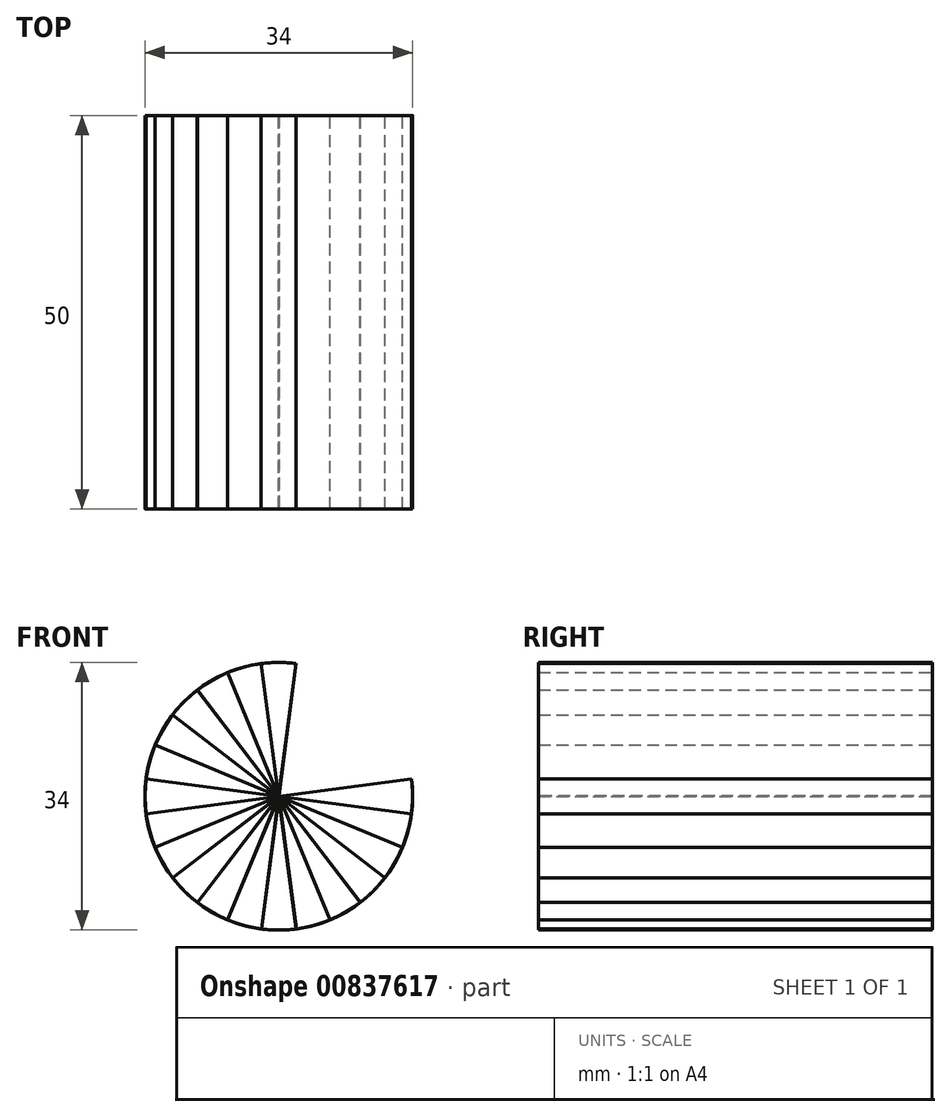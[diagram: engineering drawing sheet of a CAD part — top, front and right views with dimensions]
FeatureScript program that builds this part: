
annotation { "Feature Type Name" : "Feature", "Feature Type Description" : "" }
export const myFeature = defineFeature(function(context is Context, id is Id, definition is map)
    precondition{}
    {
        {
            var Q0;
            Q0=qCreatedBy(makeId("Front.planeOp"),FACE);
            var sketch = newSketch(context, id + "F0", { "sketchPlane" : qUnion([Q0])});
            skCircle(sketch, "E0", {"center": v(-0.33, 0) * mm, "radius": 17 * mm});
            skLineSegment(sketch, "E1", {"start": v(-0.33, 0) * mm, "end": v(-0.33, 0) * mm});
            skLineSegment(sketch, "E2.MirrorCS", {"start": v(-63.33, 0) * mm, "end": v(-17.33, 0) * mm});
            skLineSegment(sketch, "E3.MirrorCS", {"start": v(-61.33, 5.51) * mm, "end": v(-31.1, 1.5) * mm});
            skLineSegment(sketch, "E4.MirrorCS", {"start": v(-61.33, -5.5) * mm, "end": v(-31.1, -1.48) * mm});
            skArc(sketch, "E5.MirrorCS", {"start": v(-31.1, 1.5) * mm, "mid": v(-29.8, 0) * mm, "end": v(-31.1, -1.48) * mm});
            skLineSegment(sketch, "E6.MirrorCS", {"start": v(-61.33, 1.39) * mm, "end": v(-61.33, 5.51) * mm});
            skLineSegment(sketch, "E7.MirrorCS", {"start": v(-63.33, 1.39) * mm, "end": v(-61.33, 1.39) * mm});
            skLineSegment(sketch, "E8.MirrorCS", {"start": v(-63.33, -1.37) * mm, "end": v(-61.33, -1.37) * mm});
            skLineSegment(sketch, "E9.MirrorCS", {"start": v(-61.33, -1.37) * mm, "end": v(-61.33, -5.5) * mm});
            skText(sketch, "E10", { "text": "correct", "fontName": "OpenSans-Regular.ttf"});
            skLineSegment(sketch, "E11.trimOffspring", {"start": v(-17.33, 0) * mm, "end": v(-26.63, 0) * mm});
            skLineSegment(sketch, "E12", {"start": v(-0.33, 0) * mm, "end": v(54.66, 0) * mm});
            skLineSegment(sketch, "E13.MirrorCS", {"start": v(59.97, 9.34) * mm, "end": v(59.45, 13.27) * mm});
            skLineSegment(sketch, "E14.MirrorCS", {"start": v(60.33, 6.6) * mm, "end": v(60.85, 2.67) * mm});
            skLineSegment(sketch, "E15.MirrorCS", {"start": v(60.85, 2.67) * mm, "end": v(30.38, 2.55) * mm});
            skLineSegment(sketch, "E16.MirrorCS", {"start": v(59.45, 13.27) * mm, "end": v(30, 5.5) * mm});
            skArc(sketch, "E17.MirrorCS", {"start": v(30, 5.5) * mm, "mid": v(28.89, 3.86) * mm, "end": v(30.38, 2.55) * mm});
            skLineSegment(sketch, "E18.MirrorCS", {"start": v(62.13, 8.23) * mm, "end": v(-0.33, 0.01) * mm});
            skLineSegment(sketch, "E19.MirrorCS", {"start": v(61.95, 9.6) * mm, "end": v(62.31, 6.87) * mm});
            skLineSegment(sketch, "E20.MirrorCS", {"start": v(62.31, 6.87) * mm, "end": v(60.33, 6.6) * mm});
            skLineSegment(sketch, "E21.MirrorCS", {"start": v(61.95, 9.6) * mm, "end": v(59.97, 9.34) * mm});
            skLineSegment(sketch, "E22.MirrorCS", {"start": v(-0.33, 0) * mm, "end": v(-8.3, 60.49) * mm});
            skArc(sketch, "E23.MirrorCS", {"start": v(-5.82, 30.33) * mm, "mid": v(-4.18, 29.23) * mm, "end": v(-2.87, 30.72) * mm});
            skLineSegment(sketch, "E24.MirrorCS", {"start": v(-13.33, 57.8) * mm, "end": v(-5.82, 30.33) * mm});
            skLineSegment(sketch, "E25.MirrorCS", {"start": v(-2.73, 59.2) * mm, "end": v(-2.87, 30.72) * mm});
            skLineSegment(sketch, "E26.MirrorCS", {"start": v(-9.4, 58.32) * mm, "end": v(-13.33, 57.8) * mm});
            skLineSegment(sketch, "E27.MirrorCS", {"start": v(-9.66, 60.3) * mm, "end": v(-9.4, 58.32) * mm});
            skLineSegment(sketch, "E28.MirrorCS", {"start": v(-6.92, 60.67) * mm, "end": v(-6.66, 58.69) * mm});
            skLineSegment(sketch, "E29.MirrorCS", {"start": v(-6.66, 58.69) * mm, "end": v(-2.73, 59.2) * mm});
            skLineSegment(sketch, "E30", {"start": v(-0.33, 50.96) * mm, "end": v(-0.33, 0) * mm});
            skLineSegment(sketch, "E31.MirrorCS", {"start": v(2.07, 59.2) * mm, "end": v(2.21, 30.72) * mm});
            skArc(sketch, "E32.MirrorCS", {"start": v(5.16, 30.33) * mm, "mid": v(3.52, 29.23) * mm, "end": v(2.21, 30.72) * mm});
            skLineSegment(sketch, "E33.MirrorCS", {"start": v(-0.33, 0) * mm, "end": v(7.63, 60.49) * mm});
            skLineSegment(sketch, "E34.MirrorCS", {"start": v(12.67, 57.8) * mm, "end": v(5.16, 30.33) * mm});
            skLineSegment(sketch, "E35.MirrorCS", {"start": v(6, 58.69) * mm, "end": v(2.07, 59.2) * mm});
            skLineSegment(sketch, "E36.MirrorCS", {"start": v(9, 60.3) * mm, "end": v(8.74, 58.33) * mm});
            skLineSegment(sketch, "E37.MirrorCS", {"start": v(8.74, 58.33) * mm, "end": v(12.67, 57.8) * mm});
            skLineSegment(sketch, "E38.MirrorCS", {"start": v(6.26, 60.67) * mm, "end": v(6, 58.69) * mm});
            skArc(sketch, "E39", {"start": v(-6.92, 60.67) * mm, "mid": v(-0.32, 61.03) * mm, "end": v(6.28, 60.67) * mm});
            const initialGuessF0  = {"E10": [-0.0635, -0.01424, 1, 0, 0.0042]};
            skSetInitialGuess(sketch, initialGuessF0);
            skSolve(sketch);
        }
        {
            var Q0;
            {var subQ7=sQuery(id+"F0.wireOp",EDGE,"E25.MirrorCS");Q0=makeQuery(id+"F0.imprint","IMPRINT",FACE,{"disambiguationData":[TD([[makeQuery(id+"F0.imprint","IMPRINT",EDGE,{"derivedFrom":subQ7}),1.0]])]});}
            var Q1;
            {var subQ0=sQuery(id+"F0.wireOp",EDGE,"E33.MirrorCS");var subQ1=sQuery(id+"F0.wireOp",EDGE,"E0");var subQ2=makeQuery(id+"F0.imprint","INTERSECT",VERTEX,{"derivedFrom":[subQ1,subQ0]});Q1=makeQuery(id+"F0.imprint","IMPRINT",FACE,{"disambiguationData":[TD([[makeQuery(id+"F0.imprint","IMPRINT",EDGE,{"disambiguationData":[TD([[subQ2,-1.0]])],"derivedFrom":subQ1}),-1.0]])]});}
            var Q2;
            {var subQ1=sQuery(id+"F0.wireOp",EDGE,"E0");var subQ5=makeQuery(id+"F0.imprint","INTERSECT",VERTEX,{"derivedFrom":[subQ1,sQuery(id+"F0.wireOp",EDGE,"E11.trimOffspring")]});Q2=makeQuery(id+"F0.imprint","IMPRINT",FACE,{"disambiguationData":[TD([[makeQuery(id+"F0.imprint","IMPRINT",EDGE,{"disambiguationData":[TD([[subQ5,1.0]])],"derivedFrom":subQ1}),1.0]])]});}
            var Q3;
            {var subQ0=sQuery(id+"F0.wireOp",EDGE,"E30");var subQ1=sQuery(id+"F0.wireOp",EDGE,"E0");var subQ2=makeQuery(id+"F0.imprint","INTERSECT",VERTEX,{"derivedFrom":[subQ1,subQ0]});Q3=makeQuery(id+"F0.imprint","IMPRINT",FACE,{"disambiguationData":[TD([[makeQuery(id+"F0.imprint","IMPRINT",EDGE,{"disambiguationData":[TD([[subQ2,-1.0]])],"derivedFrom":subQ1}),-1.0]])]});}
            var Q4;
            {var subQ0=sQuery(id+"F0.wireOp",EDGE,"E22.MirrorCS");var subQ1=sQuery(id+"F0.wireOp",EDGE,"E0");var subQ2=makeQuery(id+"F0.imprint","INTERSECT",VERTEX,{"derivedFrom":[subQ1,subQ0]});Q4=makeQuery(id+"F0.imprint","IMPRINT",FACE,{"disambiguationData":[TD([[makeQuery(id+"F0.imprint","IMPRINT",EDGE,{"disambiguationData":[TD([[subQ2,-1.0]])],"derivedFrom":subQ1}),-1.0]])]});}
            var Q5;
            {var subQ0=sQuery(id+"F0.wireOp",EDGE,"E18.MirrorCS");var subQ1=sQuery(id+"F0.wireOp",EDGE,"E0");var subQ2=makeQuery(id+"F0.imprint","INTERSECT",VERTEX,{"derivedFrom":[subQ1,subQ0]});Q5=makeQuery(id+"F0.imprint","IMPRINT",FACE,{"disambiguationData":[TD([[makeQuery(id+"F0.imprint","IMPRINT",EDGE,{"disambiguationData":[TD([[subQ2,-1.0]])],"derivedFrom":subQ1}),-1.0]])]});}
            extrude(context, id + "F1", {"entities" : qUnion([Q0, Q1, Q2, Q3, Q4, Q5]), "endBound" : BoundingType.SYMMETRIC, "depth" : 50 * mm, "offsetDistance" : 25 * mm});
        }
        {
            var Q0;
            Q0=makeQuery(id+"F1.opExtrude","SWEPT_BODY",BODY,{"disambiguationData":[OSD([sQuery(id+"F0.wireOp",EDGE,"E0"),sQuery(id+"F0.wireOp",EDGE,"E22.MirrorCS"),sQuery(id+"F0.wireOp",EDGE,"E23.MirrorCS"),sQuery(id+"F0.wireOp",EDGE,"E25.MirrorCS"),sQuery(id+"F0.wireOp",EDGE,"E28.MirrorCS"),sQuery(id+"F0.wireOp",EDGE,"E29.MirrorCS"),sQuery(id+"F0.wireOp",EDGE,"E31.MirrorCS"),sQuery(id+"F0.wireOp",EDGE,"E32.MirrorCS"),sQuery(id+"F0.wireOp",EDGE,"E33.MirrorCS"),sQuery(id+"F0.wireOp",EDGE,"E35.MirrorCS"),sQuery(id+"F0.wireOp",EDGE,"E38.MirrorCS"),sQuery(id+"F0.wireOp",EDGE,"E39")])]});
            var Q1;
            Q1=makeQuery(id+"F1.opExtrude","SWEPT_FACE",FACE,{"disambiguationData":[OSD([sQuery(id+"F0.wireOp",EDGE,"E0")])]});
            circularPattern(context, id + "F2", {"entities" : qUnion([Q0]), "axis" : qUnion([Q1]), "angle" : 360 * degree, "instanceCount" : 24, "equalSpace" : true});
        }
        {
            var Q0;
            Q0=makeQuery(id+"F1.opExtrude","CAP_FACE",FACE,{"disambiguationData":[OSD([sQuery(id+"F0.wireOp",EDGE,"E0"),sQuery(id+"F0.wireOp",EDGE,"E0"),sQuery(id+"F0.wireOp",EDGE,"E12"),sQuery(id+"F0.wireOp",EDGE,"E18.MirrorCS"),sQuery(id+"F0.wireOp",EDGE,"E22.MirrorCS"),sQuery(id+"F0.wireOp",EDGE,"E33.MirrorCS")])],"isStart":false});
            extrude(context, id + "F3", {"entities" : qUnion([Q0]), "operationType" : NewBodyOperationType.REMOVE, "oppositeDirection" : true, "depth" : 50 * mm, "offsetDistance" : 25 * mm});
        }
    });
